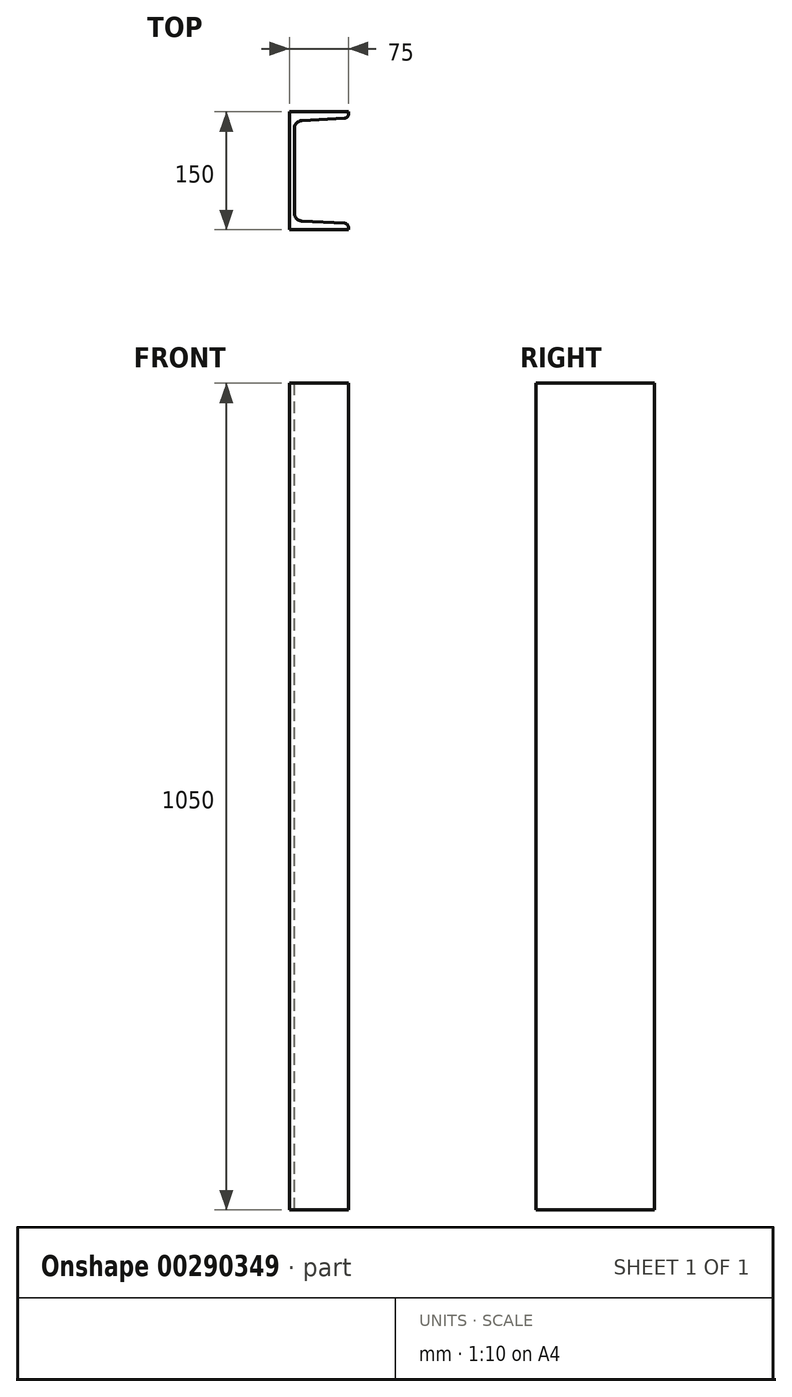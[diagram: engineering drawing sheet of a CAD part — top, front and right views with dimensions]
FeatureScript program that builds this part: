
annotation { "Feature Type Name" : "Feature", "Feature Type Description" : "" }
export const myFeature = defineFeature(function(context is Context, id is Id, definition is map)
    precondition{}
    {
        {
            var Q0;
            Q0=qCreatedBy(makeId("Top.planeOp"),FACE);
            var sketch = newSketch(context, id + "F0", { "sketchPlane" : qUnion([Q0])});
            skLineSegment(sketch, "E0", {"start": v(-184.9, -150) * mm, "end": v(-184.9, 0) * mm});
            skLineSegment(sketch, "E1", {"start": v(-184.9, 0) * mm, "end": v(-109.9, 0) * mm});
            skLineSegment(sketch, "E2", {"start": v(-109.9, 0) * mm, "end": v(-109.9, -3.29) * mm});
            skLineSegment(sketch, "E3", {"start": v(-178.4, -21.11) * mm, "end": v(-178.4, -128.89) * mm});
            skLineSegment(sketch, "E4", {"start": v(-109.9, -150) * mm, "end": v(-184.9, -150) * mm});
            skPoint(sketch, "E5", {"position": v(-147.4, -10) * mm});
            skLineSegment(sketch, "E6", {"start": v(-168.93, -11.13) * mm, "end": v(-114.64, -8.28) * mm});
            skArc(sketch, "E7.filletArc", {"start": v(-168.93, -11.13) * mm, "mid": v(-175.66, -14.23) * mm, "end": v(-178.4, -21.11) * mm});
            skPoint(sketch, "E8.visualSharp", {"position": v(-109.9, -8.03) * mm});
            skArc(sketch, "E8.filletArc", {"start": v(-114.64, -8.28) * mm, "mid": v(-111.28, -6.73) * mm, "end": v(-109.9, -3.29) * mm});
            skPoint(sketch, "E9.endSnap0", {"position": v(-184.9, -75) * mm});
            skLineSegment(sketch, "E10.MirrorCS", {"start": v(-109.9, -150) * mm, "end": v(-109.9, -146.71) * mm});
            skArc(sketch, "E11.MirrorCS", {"start": v(-114.64, -141.72) * mm, "mid": v(-111.28, -143.27) * mm, "end": v(-109.9, -146.71) * mm});
            skArc(sketch, "E12.MirrorCS", {"start": v(-168.93, -138.87) * mm, "mid": v(-175.66, -135.77) * mm, "end": v(-178.4, -128.89) * mm});
            skLineSegment(sketch, "E13.MirrorCS", {"start": v(-168.93, -138.87) * mm, "end": v(-114.64, -141.72) * mm});
            skPoint(sketch, "E14.MirrorP", {"position": v(-109.9, -141.97) * mm});
            skPoint(sketch, "E15.MirrorP", {"position": v(-147.4, -140) * mm});
            skPoint(sketch, "E9.start.orphan", {"position": v(-184.9, -75) * mm});
            skSolve(sketch);
        }
        {
            var Q0;
            Q0=makeQuery(id+"F0.imprint","IMPRINT",FACE,{"disambiguationData":[TD([[makeQuery(id+"F0.imprint","IMPRINT",EDGE,{"derivedFrom":sQuery(id+"F0.wireOp",EDGE,"E0")}),-1.0]])]});
            extrude(context, id + "F1", {"entities" : qUnion([Q0]), "oppositeDirection" : true, "depth" : 1050 * mm});
        }
    });
